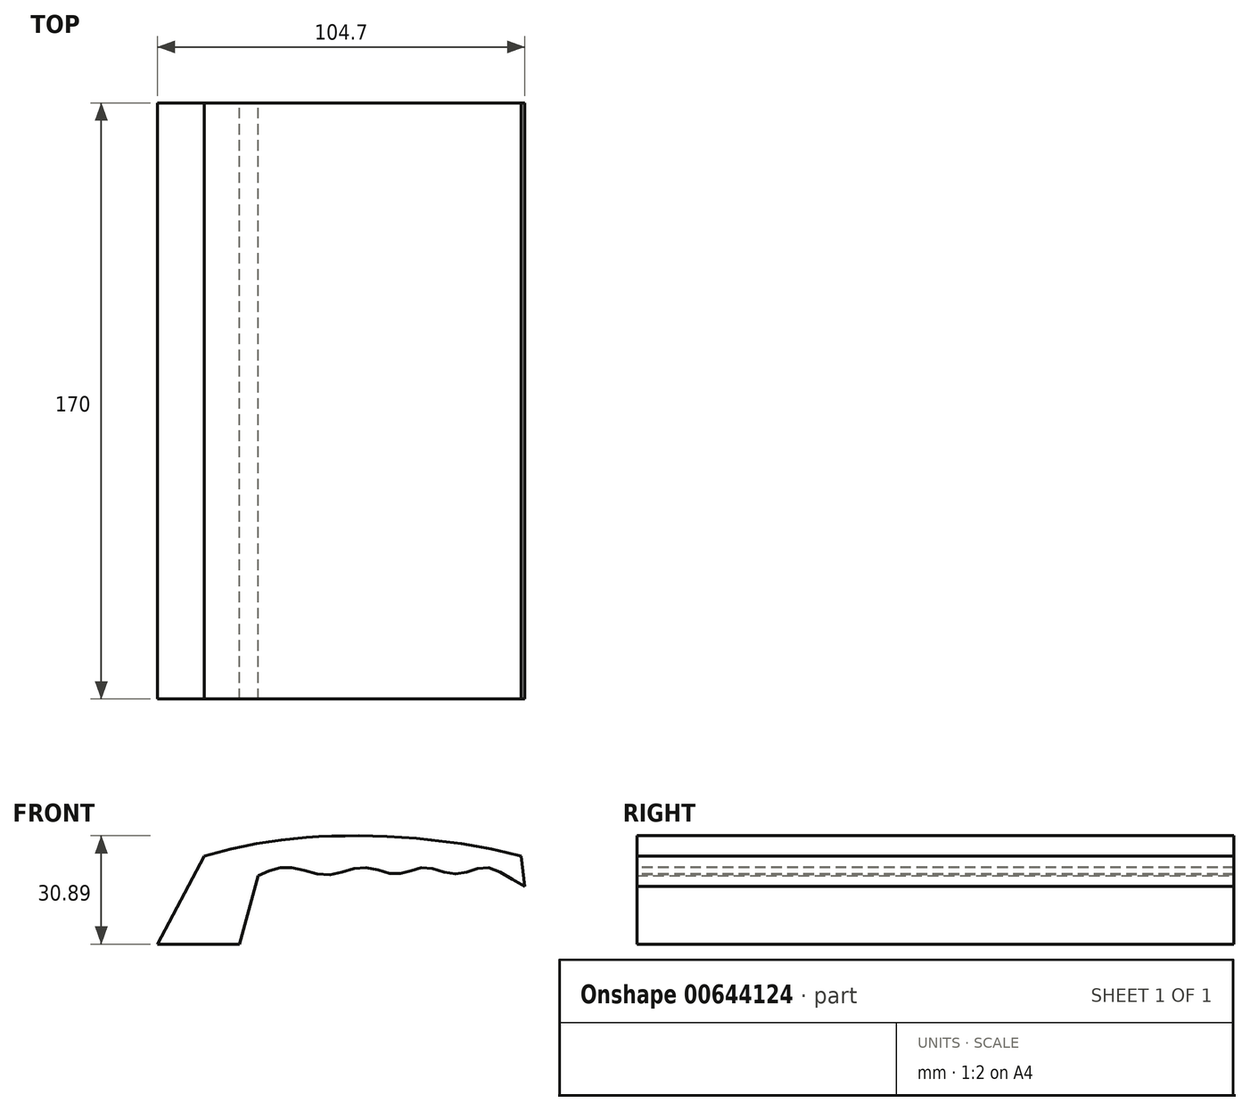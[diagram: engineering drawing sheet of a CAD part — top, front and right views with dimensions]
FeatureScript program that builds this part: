
annotation { "Feature Type Name" : "Feature", "Feature Type Description" : "" }
export const myFeature = defineFeature(function(context is Context, id is Id, definition is map)
    precondition{}
    {
        {
            var Q0;
            Q0=qCreatedBy(makeId("Front.planeOp"),FACE);
            var sketch = newSketch(context, id + "F0", { "sketchPlane" : qUnion([Q0])});
            skLineSegment(sketch, "E0", {"start": v(-39.29, 0) * mm, "end": v(-52.6, -25.09) * mm});
            skFitSpline(sketch, "E1", {"points": [v(-39.29, 0) * mm, v(0, 5.77) * mm, v(51.08, 0) * mm], "startDerivative": vector(90.62, 25.96) * mm, "endDerivative": vector(96.64, -25.61) * mm});
            skLineSegment(sketch, "E2", {"start": v(51.08, 0) * mm, "end": v(52.1, -8.67) * mm});
            skFitSpline(sketch, "E3", {"points": [v(52.1, -8.67) * mm, v(41.04, -3.24) * mm, v(32.65, -5.1) * mm, v(23.4, -3.24) * mm, v(15.74, -5.1) * mm, v(6.27, -3.24) * mm, v(-4, -5.3) * mm, v(-15.14, -3.24) * mm, v(-23.84, -5.63) * mm], "startDerivative": vector(-82.62, 39.47) * mm, "endDerivative": vector(-77.08, -37.16) * mm});
            skLineSegment(sketch, "E4", {"start": v(-23.84, -5.63) * mm, "end": v(-29.2, -25.09) * mm});
            skLineSegment(sketch, "E5", {"start": v(-52.6, -25.09) * mm, "end": v(-29.2, -25.09) * mm});
            skSolve(sketch);
        }
        {
            var Q0;
            Q0=makeQuery(id+"F0.imprint","IMPRINT",FACE,{"disambiguationData":[TD([[makeQuery(id+"F0.imprint","IMPRINT",EDGE,{"derivedFrom":sQuery(id+"F0.wireOp",EDGE,"E0")}),1.0]])]});
            extrude(context, id + "F1", {"entities" : qUnion([Q0]), "depth" : 85 * mm, "offsetDistance" : 25 * mm});
        }
        {
            var Q0;
            Q0=makeQuery(id+"F1.opExtrude","SWEPT_BODY",BODY,{"disambiguationData":[OSD([sQuery(id+"F0.wireOp",EDGE,"E0"),sQuery(id+"F0.wireOp",EDGE,"E1"),sQuery(id+"F0.wireOp",EDGE,"E2"),sQuery(id+"F0.wireOp",EDGE,"E3"),sQuery(id+"F0.wireOp",EDGE,"E4"),sQuery(id+"F0.wireOp",EDGE,"E5")])]});
            var Q1;
            Q1=qCreatedBy(makeId("Front.planeOp"),FACE);
            mirror(context, id + "F2", {"operationType" : NewBodyOperationType.ADD, "entities" : qUnion([Q0]), "mirrorPlane" : qUnion([Q1])});
        }
    });
